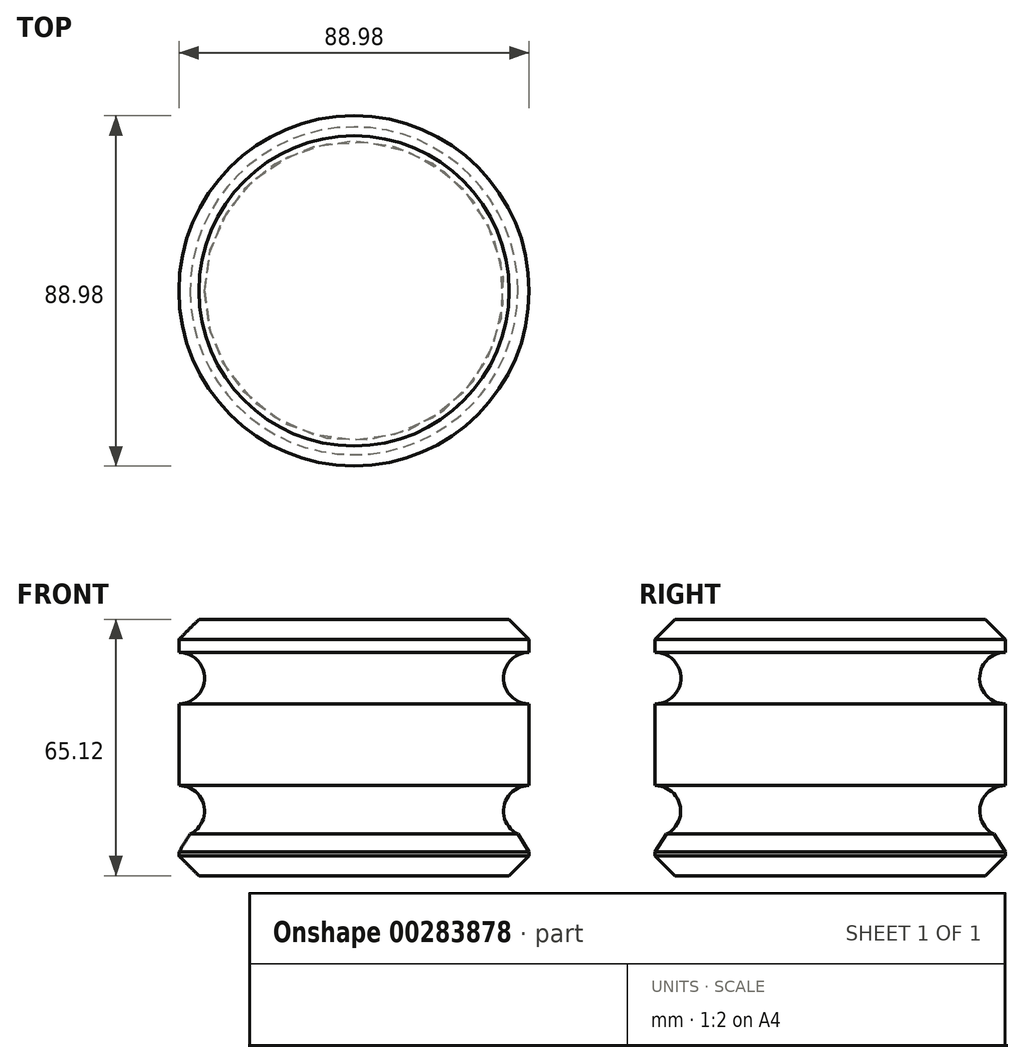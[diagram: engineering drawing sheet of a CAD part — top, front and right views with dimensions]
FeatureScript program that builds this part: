
annotation { "Feature Type Name" : "Feature", "Feature Type Description" : "" }
export const myFeature = defineFeature(function(context is Context, id is Id, definition is map)
    precondition{}
    {
        {
            var Q0;
            Q0=qCreatedBy(makeId("Front.planeOp"),FACE);
            var sketch = newSketch(context, id + "F0", { "sketchPlane" : qUnion([Q0])});
            skLineSegment(sketch, "E0.bottom", {"start": v(0, 0) * mm, "end": v(-44.5, 0) * mm});
            skLineSegment(sketch, "E0.top", {"start": v(0, 65.12) * mm, "end": v(-44.5, 65.12) * mm});
            skLineSegment(sketch, "E0.left", {"start": v(0, 0) * mm, "end": v(0, 65.12) * mm});
            skLineSegment(sketch, "E0.right", {"start": v(-44.5, 0) * mm, "end": v(-44.5, 9.92) * mm});
            skArc(sketch, "E1", {"start": v(-44.5, 43.68) * mm, "mid": v(-37.96, 50.22) * mm, "end": v(-44.5, 56.76) * mm});
            skArc(sketch, "E2", {"start": v(-44.5, 9.92) * mm, "mid": v(-37.99, 16.42) * mm, "end": v(-44.5, 22.93) * mm});
            skLineSegment(sketch, "E3.trimOffspring", {"start": v(-44.5, 56.76) * mm, "end": v(-44.5, 65.12) * mm});
            skLineSegment(sketch, "E4.trimOffspring", {"start": v(-44.5, 22.93) * mm, "end": v(-44.5, 43.68) * mm});
            skSolve(sketch);
        }
        {
            var Q0;
            Q0 = qSketchRegion(id + "F0", true);
            var Q1;
            Q1=sQuery(id+"F0.wireOp",EDGE,"E0.left");
            revolve(context, id + "F1", {"entities" : qUnion([Q0]), "axis" : qUnion([Q1]), "revolveType" : RevolveType.FULL});
        }
        {
            var Q0;
            Q0=makeQuery(id+"F1.opRevolve","SWEPT_EDGE",EDGE,{"disambiguationData":[OSD([sQuery(id+"F0.wireOp",EDGE,"E0.top"),sQuery(id+"F0.wireOp",EDGE,"E3.trimOffspring")])]});
            var Q1;
            Q1=makeQuery(id+"F1.opRevolve","SWEPT_FACE",FACE,{"disambiguationData":[OSD([sQuery(id+"F0.wireOp",EDGE,"E0.right")])]});
            chamfer(context, id + "F2", {"entities" : qUnion([Q0, Q1]), "width" : 5.08 * mm, "tangentPropagation" : true});
        }
    });
